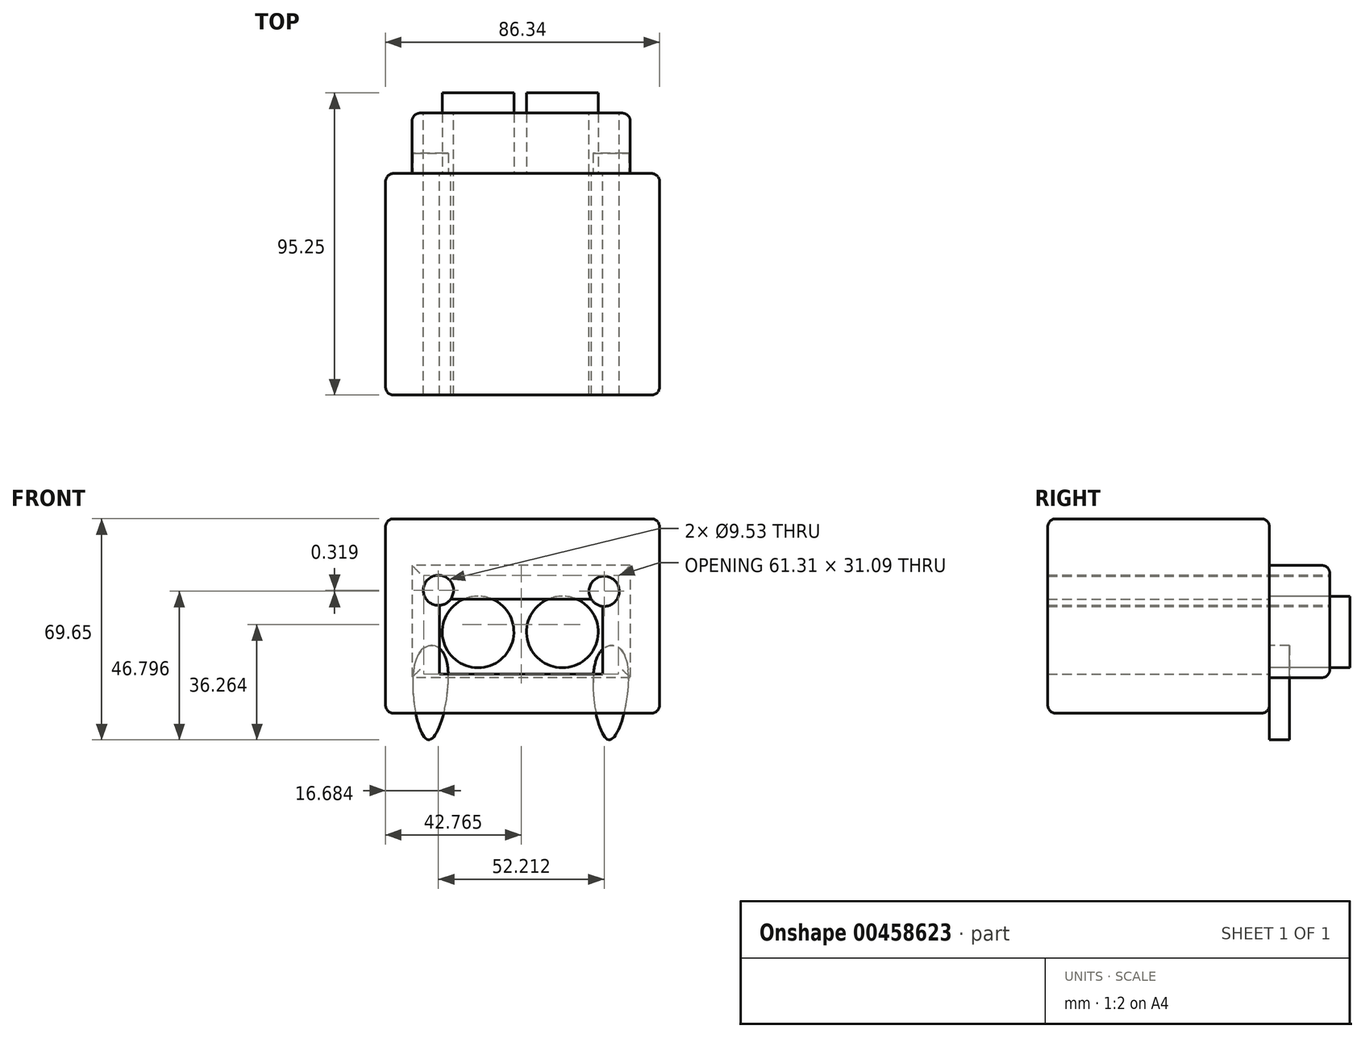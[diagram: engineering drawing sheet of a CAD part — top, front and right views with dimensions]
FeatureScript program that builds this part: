
annotation { "Feature Type Name" : "Feature", "Feature Type Description" : "" }
export const myFeature = defineFeature(function(context is Context, id is Id, definition is map)
    precondition{}
    {
        {
            var Q0;
            Q0=qCreatedBy(makeId("Front.planeOp"),FACE);
            var sketch = newSketch(context, id + "F0", { "sketchPlane" : qUnion([Q0])});
            skCircle(sketch, "E0", {"center": v(-13.14, 0) * mm, "radius": 11.29 * mm});
            skCircle(sketch, "E1", {"center": v(13.43, 0) * mm, "radius": 11.29 * mm});
            skSolve(sketch);
        }
        {
            var Q0;
            Q0=qCreatedBy(makeId("Front.planeOp"),FACE);
            var sketch = newSketch(context, id + "F1", { "sketchPlane" : qUnion([Q0])});
            skLineSegment(sketch, "E2.bottom", {"start": v(44.03, 35.69) * mm, "end": v(-42.3, 35.69) * mm});
            skLineSegment(sketch, "E2.top", {"start": v(44.03, -25.61) * mm, "end": v(-42.3, -25.61) * mm});
            skLineSegment(sketch, "E2.left", {"start": v(44.03, 35.69) * mm, "end": v(44.03, -25.61) * mm});
            skLineSegment(sketch, "E2.right", {"start": v(-42.3, 35.69) * mm, "end": v(-42.3, -25.61) * mm});
            skSolve(sketch);
        }
        {
            var Q0;
            Q0 = qSketchRegion(id + "F1", true);
            extrude(context, id + "F2", {"entities" : qUnion([Q0]), "depth" : 69.85 * mm});
        }
        {
            var Q0;
            Q0=qCreatedBy(makeId("Front.planeOp"),FACE);
            var sketch = newSketch(context, id + "F3", { "sketchPlane" : qUnion([Q0])});
            skLineSegment(sketch, "E3.bottom", {"start": v(34.82, 21) * mm, "end": v(-33.96, 21) * mm});
            skLineSegment(sketch, "E3.top", {"start": v(34.82, -14.4) * mm, "end": v(-33.96, -14.4) * mm});
            skLineSegment(sketch, "E3.left", {"start": v(34.82, 21) * mm, "end": v(34.82, -14.4) * mm});
            skLineSegment(sketch, "E3.right", {"start": v(-33.96, 21) * mm, "end": v(-33.96, -14.4) * mm});
            skSolve(sketch);
        }
        {
            var Q0;
            Q0=qCreatedBy(makeId("Front.planeOp"),FACE);
            var sketch = newSketch(context, id + "F4", { "sketchPlane" : qUnion([Q0])});
            skFitSpline(sketch, "E4", {"points": [v(33.1, -7.2) * mm, v(24.75, -7.2) * mm, v(28.2, -33.96) * mm, v(33.1, -7.2) * mm]});
            skFitSpline(sketch, "E5", {"points": [v(-23.73, -7.2) * mm, v(-32.08, -7.2) * mm, v(-28.63, -33.96) * mm, v(-23.73, -7.2) * mm]});
            skSolve(sketch);
        }
        {
            var Q0;
            Q0 = qSketchRegion(id + "F0", true);
            extrude(context, id + "F5", {"entities" : qUnion([Q0]), "oppositeDirection" : true, "depth" : 25.4 * mm});
        }
        {
            var Q0;
            Q0 = qSketchRegion(id + "F4", true);
            extrude(context, id + "F6", {"entities" : qUnion([Q0]), "oppositeDirection" : true, "depth" : 6.35 * mm});
        }
        {
            var Q0;
            Q0=makeQuery(id+"F3.imprint","IMPRINT",FACE,{"disambiguationData":[TD([[makeQuery(id+"F3.imprint","IMPRINT",EDGE,{"derivedFrom":sQuery(id+"F3.wireOp",EDGE,"E3.bottom")}),1.0]])]});
            extrude(context, id + "F7", {"entities" : qUnion([Q0]), "oppositeDirection" : true, "depth" : 19.05 * mm});
        }
        {
            var Q0;
            Q0=makeQuery(id+"F2.opExtrude","SWEPT_EDGE",EDGE,{"disambiguationData":[OSD([sQuery(id+"F1.wireOp",EDGE,"E2.bottom"),sQuery(id+"F1.wireOp",EDGE,"E2.right")])]});
            var Q1;
            Q1=makeQuery(id+"F2.opExtrude","CAP_EDGE",EDGE,{"disambiguationData":[OSD([sQuery(id+"F1.wireOp",EDGE,"E2.bottom")])],"isStart":true});
            var Q2;
            Q2=makeQuery(id+"F2.opExtrude","SWEPT_EDGE",EDGE,{"disambiguationData":[OSD([sQuery(id+"F1.wireOp",EDGE,"E2.bottom"),sQuery(id+"F1.wireOp",EDGE,"E2.left")])]});
            var Q3;
            Q3=makeQuery(id+"F2.opExtrude","CAP_EDGE",EDGE,{"disambiguationData":[OSD([sQuery(id+"F1.wireOp",EDGE,"E2.bottom")])],"isStart":false});
            var Q4;
            Q4=makeQuery(id+"F2.opExtrude","CAP_FACE",FACE,{"disambiguationData":[OSD([sQuery(id+"F1.wireOp",EDGE,"E2.bottom"),sQuery(id+"F1.wireOp",EDGE,"E2.top"),sQuery(id+"F1.wireOp",EDGE,"E2.left"),sQuery(id+"F1.wireOp",EDGE,"E2.right")])],"isStart":false});
            var Q5;
            Q5=makeQuery(id+"F2.opExtrude","CAP_EDGE",EDGE,{"disambiguationData":[OSD([sQuery(id+"F1.wireOp",EDGE,"E2.right")])],"isStart":false});
            var Q6;
            Q6=makeQuery(id+"F2.opExtrude","SWEPT_EDGE",EDGE,{"disambiguationData":[OSD([sQuery(id+"F1.wireOp",EDGE,"E2.top"),sQuery(id+"F1.wireOp",EDGE,"E2.left")])]});
            var Q7;
            Q7=makeQuery(id+"F2.opExtrude","SWEPT_FACE",FACE,{"disambiguationData":[OSD([sQuery(id+"F1.wireOp",EDGE,"E2.left")])]});
            var Q8;
            Q8=makeQuery(id+"F7.opExtrude","CAP_EDGE",EDGE,{"disambiguationData":[OSD([sQuery(id+"F3.wireOp",EDGE,"E3.bottom")])],"isStart":false});
            var Q9;
            Q9=makeQuery(id+"F7.opExtrude","CAP_EDGE",EDGE,{"disambiguationData":[OSD([sQuery(id+"F3.wireOp",EDGE,"E3.right")])],"isStart":false});
            var Q10;
            Q10=makeQuery(id+"F7.opExtrude","CAP_EDGE",EDGE,{"disambiguationData":[OSD([sQuery(id+"F3.wireOp",EDGE,"E3.top")])],"isStart":false});
            var Q11;
            Q11=makeQuery(id+"F7.opExtrude","CAP_EDGE",EDGE,{"disambiguationData":[OSD([sQuery(id+"F3.wireOp",EDGE,"E3.left")])],"isStart":false});
            fillet(context, id + "F8", {"entities" : qUnion([Q0, Q1, Q2, Q3, Q4, Q5, Q6, Q7, Q8, Q9, Q10, Q11]), "radius" : 2.54 * mm, "tangentPropagation" : true, "allowEdgeOverflow" : false});
        }
        {
            var Q0;
            Q0=makeQuery(id+"F2.opExtrude","CAP_EDGE",EDGE,{"disambiguationData":[OSD([sQuery(id+"F1.wireOp",EDGE,"E2.right")])],"isStart":true});
            var Q1;
            Q1=makeQuery(id+"F2.opExtrude","CAP_EDGE",EDGE,{"disambiguationData":[OSD([sQuery(id+"F1.wireOp",EDGE,"E2.top")])],"isStart":true});
            fillet(context, id + "F9", {"entities" : qUnion([Q0, Q1]), "radius" : 2.54 * mm, "tangentPropagation" : true, "allowEdgeOverflow" : false});
        }
        {
            var Q0;
            Q0=makeQuery(id+"F2.opExtrude","SWEPT_EDGE",EDGE,{"disambiguationData":[OSD([sQuery(id+"F1.wireOp",EDGE,"E2.top"),sQuery(id+"F1.wireOp",EDGE,"E2.right")])]});
            fillet(context, id + "F10", {"entities" : qUnion([Q0]), "radius" : 2.54 * mm, "tangentPropagation" : true, "allowEdgeOverflow" : false});
        }
        {
            var Q0;
            Q0=qCreatedBy(makeId("Front.planeOp"),FACE);
            var sketch = newSketch(context, id + "F11", { "sketchPlane" : qUnion([Q0])});
            skCircle(sketch, "E6", {"center": v(26.59, 12.84) * mm, "radius": 4.76 * mm});
            skCircle(sketch, "E7", {"center": v(-25.63, 13.16) * mm, "radius": 4.76 * mm});
            skSolve(sketch);
        }
        {
            var Q0;
            Q0 = qSketchRegion(id + "F11", true);
            extrude(context, id + "F12", {"entities" : qUnion([Q0]), "operationType" : NewBodyOperationType.REMOVE, "endBound" : BoundingType.SYMMETRIC, "depth" : 558.8 * mm});
        }
        {
            var Q0;
            Q0=qCreatedBy(makeId("Front.planeOp"),FACE);
            var sketch = newSketch(context, id + "F13", { "sketchPlane" : qUnion([Q0])});
            skLineSegment(sketch, "E8.bottom", {"start": v(-25.33, 10.36) * mm, "end": v(26.2, 10.36) * mm});
            skLineSegment(sketch, "E8.top", {"start": v(-25.33, -13.24) * mm, "end": v(26.2, -13.24) * mm});
            skLineSegment(sketch, "E8.left", {"start": v(-25.33, 10.36) * mm, "end": v(-25.33, -13.24) * mm});
            skLineSegment(sketch, "E8.right", {"start": v(26.2, 10.36) * mm, "end": v(26.2, -13.24) * mm});
            skSolve(sketch);
        }
        {
            var Q0;
            Q0 = qSketchRegion(id + "F13", true);
            extrude(context, id + "F14", {"entities" : qUnion([Q0]), "operationType" : NewBodyOperationType.REMOVE, "depth" : 101.6 * mm});
        }
    });
